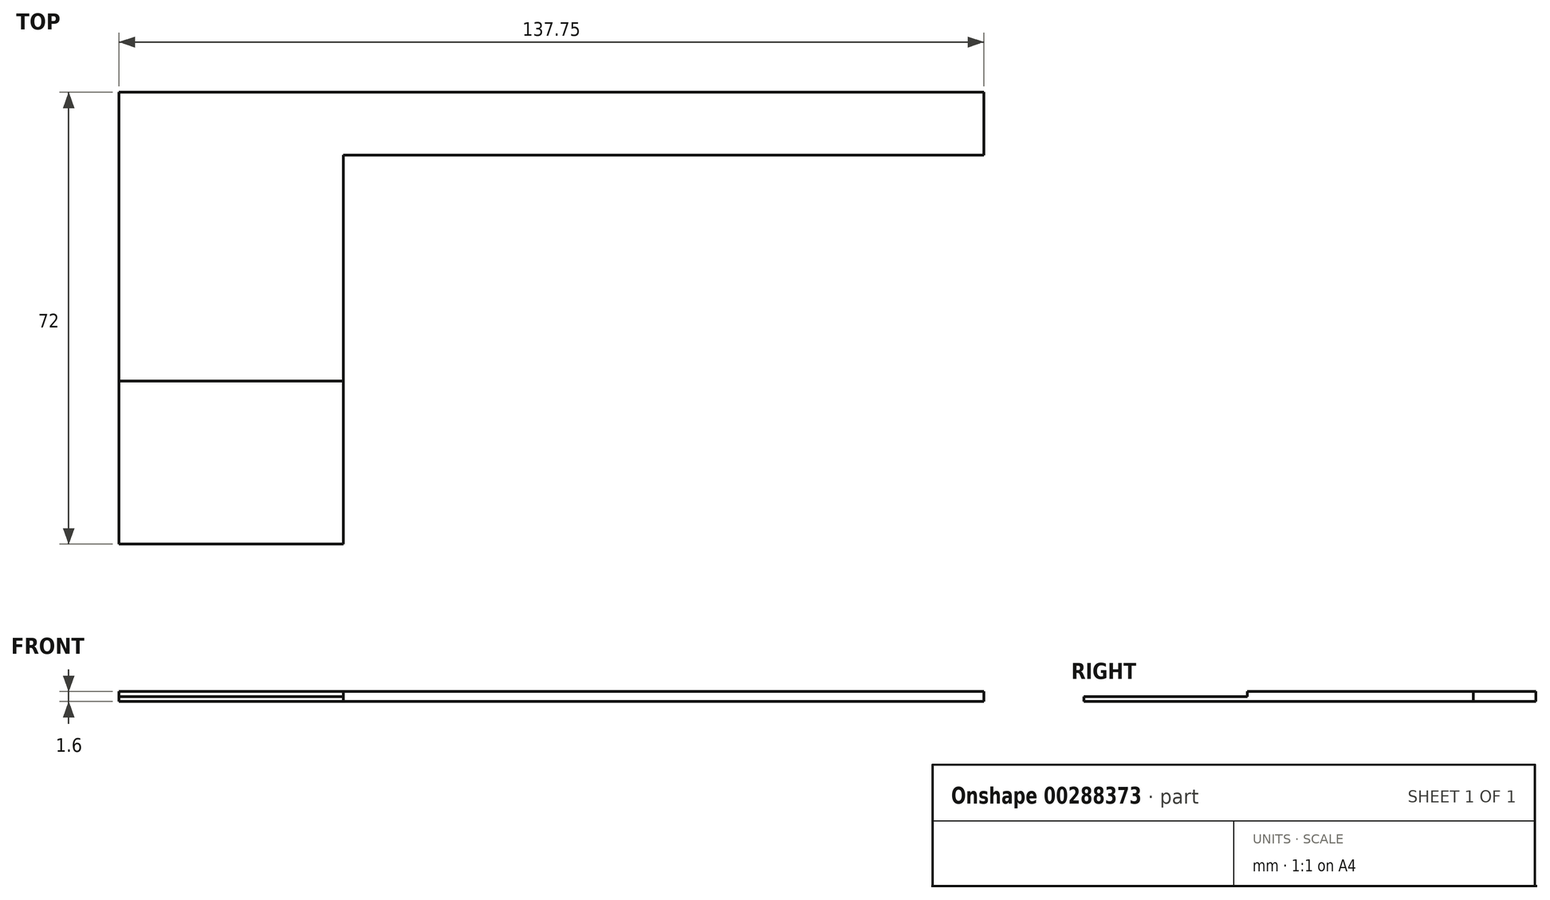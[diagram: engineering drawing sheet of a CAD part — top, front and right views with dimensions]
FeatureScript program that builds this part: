
annotation { "Feature Type Name" : "Feature", "Feature Type Description" : "" }
export const myFeature = defineFeature(function(context is Context, id is Id, definition is map)
    precondition{}
    {
        {
            var Q0;
            Q0=qCreatedBy(makeId("Top.planeOp"),FACE);
            var sketch = newSketch(context, id + "F0", { "sketchPlane" : qUnion([Q0])});
            skLineSegment(sketch, "E0.bottom", {"start": v(0, 0) * mm, "end": v(35.75, 0) * mm});
            skLineSegment(sketch, "E0.top", {"start": v(0, 72) * mm, "end": v(137.75, 72) * mm});
            skLineSegment(sketch, "E0.left", {"start": v(0, 0) * mm, "end": v(0, 72) * mm});
            skLineSegment(sketch, "E0.right", {"start": v(137.75, 62) * mm, "end": v(137.75, 72) * mm});
            skLineSegment(sketch, "E1", {"start": v(35.75, 0) * mm, "end": v(35.75, 62) * mm});
            skLineSegment(sketch, "E2", {"start": v(35.75, 62) * mm, "end": v(137.75, 62) * mm});
            skPoint(sketch, "E3.orphan", {"position": v(137.75, 0) * mm});
            skSolve(sketch);
        }
        {
            var Q0;
            Q0 = qSketchRegion(id + "F0", true);
            extrude(context, id + "F1", {"entities" : qUnion([Q0]), "depth" : 0.8 * mm, "offsetDistance" : 25 * mm});
        }
        {
            var Q0;
            Q0=makeQuery(id+"F1.opExtrude","CAP_FACE",FACE,{"disambiguationData":[OSD([sQuery(id+"F0.wireOp",EDGE,"E0.bottom"),sQuery(id+"F0.wireOp",EDGE,"E0.top"),sQuery(id+"F0.wireOp",EDGE,"E0.left"),sQuery(id+"F0.wireOp",EDGE,"E0.right"),sQuery(id+"F0.wireOp",EDGE,"E1"),sQuery(id+"F0.wireOp",EDGE,"E2")])],"isStart":false});
            var sketch = newSketch(context, id + "F2", { "sketchPlane" : qUnion([Q0])});
            skLineSegment(sketch, "E4", {"start": v(0, 26) * mm, "end": v(35.75, 26) * mm});
            skSolve(sketch);
        }
        {
            var Q0;
            Q0 = qSketchRegion(id + "F2", true);
            var Q1;
            {var subQ2=sQuery(id+"F2.wireOp",EDGE,"E4");Q1=makeQuery(id+"F2.imprint","IMPRINT",FACE,{"disambiguationData":[TD([[makeQuery(id+"F2.imprint","IMPRINT",EDGE,{"derivedFrom":subQ2}),1.0]])]});}
            extrude(context, id + "F3", {"entities" : qUnion([Q0, Q1]), "operationType" : NewBodyOperationType.ADD, "depth" : 0.8 * mm, "offsetDistance" : 25 * mm});
        }
    });
